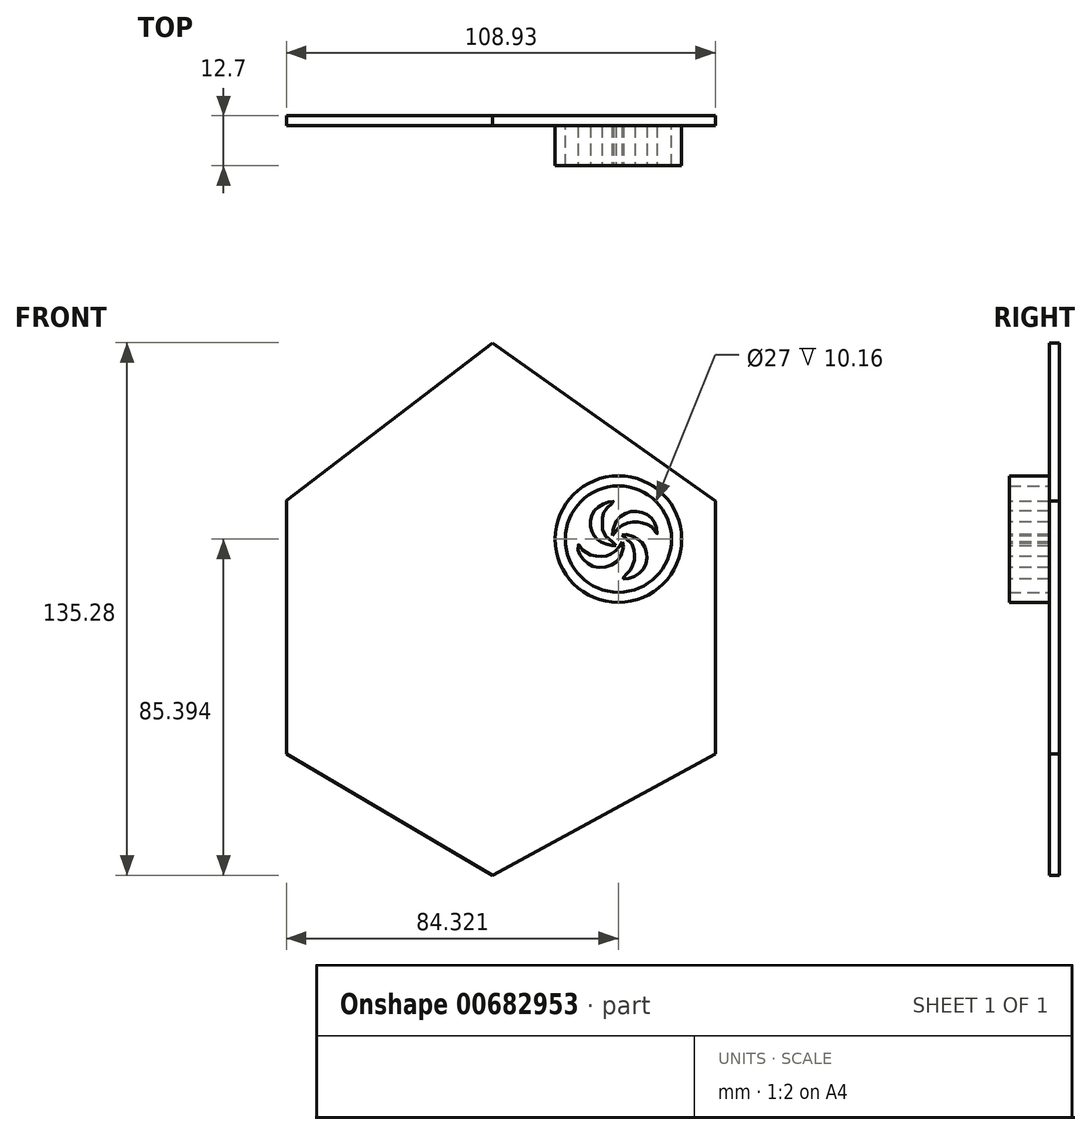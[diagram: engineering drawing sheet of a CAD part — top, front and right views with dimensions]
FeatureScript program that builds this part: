
annotation { "Feature Type Name" : "Feature", "Feature Type Description" : "" }
export const myFeature = defineFeature(function(context is Context, id is Id, definition is map)
    precondition{}
    {
        {
            var Q0;
            Q0=qCreatedBy(makeId("Front.planeOp"),FACE);
            var sketch = newSketch(context, id + "F0", { "sketchPlane" : qUnion([Q0])});
            skLineSegment(sketch, "E0", {"start": v(0, 68.56) * mm, "end": v(59.23, 26.56) * mm});
            skLineSegment(sketch, "E1", {"start": v(59.23, 26.56) * mm, "end": v(59.23, -40.56) * mm});
            skLineSegment(sketch, "E2", {"start": v(59.23, -40.56) * mm, "end": v(0, -72.79) * mm});
            skLineSegment(sketch, "E3", {"start": v(0, -72.79) * mm, "end": v(-54.78, -40.56) * mm});
            skLineSegment(sketch, "E4", {"start": v(-54.78, -40.56) * mm, "end": v(-54.78, 26.56) * mm});
            skLineSegment(sketch, "E5", {"start": v(-54.78, 26.56) * mm, "end": v(0, 68.56) * mm});
            skSolve(sketch);
        }
        {
            var Q0;
            Q0=makeQuery(id+"F0.imprint","IMPRINT",FACE,{"disambiguationData":[TD([[makeQuery(id+"F0.imprint","IMPRINT",EDGE,{"derivedFrom":sQuery(id+"F0.wireOp",EDGE,"E0")}),-1.0]])]});
            extrude(context, id + "F1", {"entities" : qUnion([Q0]), "depth" : 12.7 * mm, "offsetDistance" : 25.4 * mm});
        }
        {
            var Q0;
            Q0=makeQuery(id+"F1.opExtrude","CAP_FACE",FACE,{"disambiguationData":[OSD([sQuery(id+"F0.wireOp",EDGE,"E0"),sQuery(id+"F0.wireOp",EDGE,"E1"),sQuery(id+"F0.wireOp",EDGE,"E2"),sQuery(id+"F0.wireOp",EDGE,"E3"),sQuery(id+"F0.wireOp",EDGE,"E4"),sQuery(id+"F0.wireOp",EDGE,"E5")])],"isStart":false});
            extrude(context, id + "F2", {"entities" : qUnion([Q0]), "operationType" : NewBodyOperationType.REMOVE, "oppositeDirection" : true, "depth" : 2.54 * mm, "offsetDistance" : 25.4 * mm});
        }
        {
            var Q0;
            Q0=makeQuery(id+"F2.boolean.opBoolean","COPY",FACE,{"derivedFrom":makeQuery(id+"F2.opExtrude","CAP_FACE",FACE,{"disambiguationData":[OSD([sQuery(id+"F0.wireOp",EDGE,"E0"),sQuery(id+"F0.wireOp",EDGE,"E1"),sQuery(id+"F0.wireOp",EDGE,"E2"),sQuery(id+"F0.wireOp",EDGE,"E3"),sQuery(id+"F0.wireOp",EDGE,"E4"),sQuery(id+"F0.wireOp",EDGE,"E5")])],"isStart":false})});
            extrude(context, id + "F3", {"entities" : qUnion([Q0]), "operationType" : NewBodyOperationType.REMOVE, "oppositeDirection" : true, "depth" : 7.62 * mm, "offsetDistance" : 25.4 * mm});
        }
        {
            var Q0;
            Q0=makeQuery(id+"F1.opExtrude","SWEPT_FACE",FACE,{"disambiguationData":[OSD([sQuery(id+"F0.wireOp",EDGE,"E0")])]});
            extrude(context, id + "F4", {"entities" : qUnion([Q0]), "operationType" : NewBodyOperationType.REMOVE, "oppositeDirection" : true, "depth" : 2.54 * mm, "offsetDistance" : 25.4 * mm});
        }
        {
            var Q0;
            Q0=makeQuery(id+"F1.opExtrude","SWEPT_FACE",FACE,{"disambiguationData":[OSD([sQuery(id+"F0.wireOp",EDGE,"E5")])]});
            extrude(context, id + "F5", {"entities" : qUnion([Q0]), "operationType" : NewBodyOperationType.REMOVE, "oppositeDirection" : true, "depth" : 2.54 * mm, "offsetDistance" : 25.4 * mm});
        }
        {
            var Q0;
            Q0=makeQuery(id+"F1.opExtrude","SWEPT_FACE",FACE,{"disambiguationData":[OSD([sQuery(id+"F0.wireOp",EDGE,"E1")])]});
            extrude(context, id + "F6", {"entities" : qUnion([Q0]), "operationType" : NewBodyOperationType.REMOVE, "oppositeDirection" : true, "depth" : 2.54 * mm, "offsetDistance" : 25.4 * mm});
        }
        {
            var Q0;
            Q0=makeQuery(id+"F1.opExtrude","SWEPT_FACE",FACE,{"disambiguationData":[OSD([sQuery(id+"F0.wireOp",EDGE,"E4")])]});
            extrude(context, id + "F7", {"entities" : qUnion([Q0]), "operationType" : NewBodyOperationType.REMOVE, "oppositeDirection" : true, "depth" : 2.54 * mm, "offsetDistance" : 25.4 * mm});
        }
        {
            var Q0;
            Q0=makeQuery(id+"F1.opExtrude","SWEPT_FACE",FACE,{"disambiguationData":[OSD([sQuery(id+"F0.wireOp",EDGE,"E3")])]});
            extrude(context, id + "F8", {"entities" : qUnion([Q0]), "operationType" : NewBodyOperationType.REMOVE, "oppositeDirection" : true, "depth" : 2.54 * mm, "offsetDistance" : 25.4 * mm});
        }
        {
            var Q0;
            Q0=makeQuery(id+"F1.opExtrude","SWEPT_FACE",FACE,{"disambiguationData":[OSD([sQuery(id+"F0.wireOp",EDGE,"E2")])]});
            extrude(context, id + "F9", {"entities" : qUnion([Q0]), "operationType" : NewBodyOperationType.REMOVE, "oppositeDirection" : true, "depth" : 2.54 * mm, "offsetDistance" : 25.4 * mm});
        }
        {
            var Q0;
            Q0=makeQuery(id+"F3.boolean.opBoolean","COPY",FACE,{"derivedFrom":makeQuery(id+"F3.opExtrude","CAP_FACE",FACE,{"disambiguationData":[OSD([sQuery(id+"F0.wireOp",EDGE,"E0"),sQuery(id+"F0.wireOp",EDGE,"E1"),sQuery(id+"F0.wireOp",EDGE,"E2"),sQuery(id+"F0.wireOp",EDGE,"E3"),sQuery(id+"F0.wireOp",EDGE,"E4"),sQuery(id+"F0.wireOp",EDGE,"E5")])],"isStart":false})});
            var sketch = newSketch(context, id + "F10", { "sketchPlane" : qUnion([Q0])});
            skCircle(sketch, "E6", {"center": v(32.08, 15.52) * mm, "radius": 16.07 * mm});
            skCircle(sketch, "E7", {"center": v(32.08, 15.52) * mm, "radius": 13.5 * mm});
            skFitSpline(sketch, "E8", {"points": [v(31.43, 13.96) * mm, v(28.75, 16.4) * mm, v(27.96, 19.23) * mm, v(28.13, 21.52) * mm, v(29.24, 23.54) * mm, v(30.84, 24.99) * mm, v(30.08, 25.06) * mm, v(28.1, 24.3) * mm, v(26.32, 23.06) * mm, v(25.25, 21.3) * mm, v(24.99, 18.94) * mm, v(25.48, 17.15) * mm, v(26.3, 15.9) * mm, v(27.8, 14.74) * mm, v(29.95, 13.98) * mm, v(31.43, 13.96) * mm]});
            skFitSpline(sketch, "E9", {"points": [v(30.55, 16.4) * mm, v(31.33, 19.9) * mm, v(33.44, 21.77) * mm, v(35.5, 22.56) * mm, v(37.63, 22.42) * mm, v(39.46, 21.7) * mm, v(40.97, 20.3) * mm, v(41.74, 18.34) * mm, v(41.85, 16.77) * mm, v(41.06, 18.12) * mm, v(39.43, 19.25) * mm, v(37.72, 19.79) * mm, v(36.1, 19.9) * mm, v(34.17, 19.53) * mm, v(32.33, 18.58) * mm, v(31.15, 17.16) * mm, v(30.55, 16.4) * mm]});
            skFitSpline(sketch, "E10", {"points": [v(33, 16.56) * mm, v(35.31, 14.55) * mm, v(36.1, 12.1) * mm, v(36.22, 10.58) * mm, v(35.5, 8.43) * mm, v(34.64, 7.13) * mm, v(33.36, 5.84) * mm, v(33.18, 5.54) * mm, v(34.25, 5.43) * mm, v(36.68, 6.3) * mm, v(38.38, 7.95) * mm, v(39.25, 10.1) * mm, v(39.23, 11.95) * mm, v(38.41, 14.19) * mm, v(36.95, 15.52) * mm, v(34.75, 16.52) * mm, v(33, 16.56) * mm]});
            skFitSpline(sketch, "E11", {"points": [v(33.16, 14.81) * mm, v(33, 11.89) * mm, v(30.9, 9.24) * mm, v(28.4, 8.42) * mm, v(25.92, 8.54) * mm, v(23.97, 9.61) * mm, v(22.46, 11.42) * mm, v(21.82, 12.96) * mm, v(22, 14.36) * mm, v(22.52, 13.25) * mm, v(23.73, 12.24) * mm, v(25.01, 11.5) * mm, v(26.95, 11.14) * mm, v(28.67, 11.19) * mm, v(30.36, 11.82) * mm, v(31.94, 13.06) * mm, v(33.16, 14.81) * mm]});
            skSolve(sketch);
        }
        {
            var Q0;
            Q0=makeQuery(id+"F10.imprint","IMPRINT",FACE,{"disambiguationData":[TD([[makeQuery(id+"F10.imprint","IMPRINT",EDGE,{"derivedFrom":sQuery(id+"F10.wireOp",EDGE,"E6")}),1.0]])]});
            var Q1;
            Q1=makeQuery(id+"F10.imprint","IMPRINT",FACE,{"disambiguationData":[TD([[makeQuery(id+"F10.imprint","IMPRINT",EDGE,{"derivedFrom":sQuery(id+"F10.wireOp",EDGE,"E9")}),-1.0]])]});
            var Q2;
            Q2=makeQuery(id+"F10.imprint","IMPRINT",FACE,{"disambiguationData":[TD([[makeQuery(id+"F10.imprint","IMPRINT",EDGE,{"derivedFrom":sQuery(id+"F10.wireOp",EDGE,"E10")}),1.0]])]});
            var Q3;
            Q3=makeQuery(id+"F10.imprint","IMPRINT",FACE,{"disambiguationData":[TD([[makeQuery(id+"F10.imprint","IMPRINT",EDGE,{"derivedFrom":sQuery(id+"F10.wireOp",EDGE,"E11")}),-1.0]])]});
            var Q4;
            Q4=makeQuery(id+"F10.imprint","IMPRINT",FACE,{"disambiguationData":[TD([[makeQuery(id+"F10.imprint","IMPRINT",EDGE,{"derivedFrom":sQuery(id+"F10.wireOp",EDGE,"E8")}),1.0]])]});
            extrude(context, id + "F11", {"entities" : qUnion([Q0, Q1, Q2, Q3, Q4]), "operationType" : NewBodyOperationType.ADD, "depth" : 6.35 * mm, "offsetDistance" : 25.4 * mm});
        }
        {
            var Q0;
            Q0=makeQuery(id+"F11.opExtrude","CAP_FACE",FACE,{"disambiguationData":[OSD([sQuery(id+"F10.wireOp",EDGE,"E6"),sQuery(id+"F10.wireOp",EDGE,"E7")])],"isStart":false});
            var Q1;
            Q1=makeQuery(id+"F11.opExtrude","CAP_FACE",FACE,{"disambiguationData":[OSD([sQuery(id+"F10.wireOp",EDGE,"E9")])],"isStart":false});
            var Q2;
            Q2=makeQuery(id+"F11.opExtrude","CAP_FACE",FACE,{"disambiguationData":[OSD([sQuery(id+"F10.wireOp",EDGE,"E10")])],"isStart":false});
            var Q3;
            Q3=makeQuery(id+"F11.opExtrude","CAP_FACE",FACE,{"disambiguationData":[OSD([sQuery(id+"F10.wireOp",EDGE,"E11")])],"isStart":false});
            var Q4;
            Q4=makeQuery(id+"F11.opExtrude","CAP_FACE",FACE,{"disambiguationData":[OSD([sQuery(id+"F10.wireOp",EDGE,"E8")])],"isStart":false});
            extrude(context, id + "F12", {"entities" : qUnion([Q0, Q1, Q2, Q3, Q4]), "operationType" : NewBodyOperationType.ADD, "depth" : 2.54 * mm, "offsetDistance" : 25.4 * mm});
        }
        {
            var Q0;
            Q0=makeQuery(id+"F12.opExtrude","CAP_FACE",FACE,{"disambiguationData":[OSD([sQuery(id+"F10.wireOp",EDGE,"E6"),sQuery(id+"F10.wireOp",EDGE,"E7")])],"isStart":false});
            var Q1;
            Q1=makeQuery(id+"F12.opExtrude","CAP_FACE",FACE,{"disambiguationData":[OSD([sQuery(id+"F10.wireOp",EDGE,"E11")])],"isStart":false});
            var Q2;
            Q2=makeQuery(id+"F12.opExtrude","CAP_FACE",FACE,{"disambiguationData":[OSD([sQuery(id+"F10.wireOp",EDGE,"E8")])],"isStart":false});
            var Q3;
            Q3=makeQuery(id+"F12.opExtrude","CAP_FACE",FACE,{"disambiguationData":[OSD([sQuery(id+"F10.wireOp",EDGE,"E9")])],"isStart":false});
            var Q4;
            Q4=makeQuery(id+"F12.opExtrude","CAP_FACE",FACE,{"disambiguationData":[OSD([sQuery(id+"F10.wireOp",EDGE,"E10")])],"isStart":false});
            extrude(context, id + "F13", {"entities" : qUnion([Q0, Q1, Q2, Q3, Q4]), "operationType" : NewBodyOperationType.ADD, "depth" : 12.7 * mm, "offsetDistance" : 25.4 * mm});
        }
        {
            var Q0;
            Q0=makeQuery(id+"F13.opExtrude","CAP_FACE",FACE,{"disambiguationData":[OSD([sQuery(id+"F10.wireOp",EDGE,"E6"),sQuery(id+"F10.wireOp",EDGE,"E7")])],"isStart":false});
            var Q1;
            Q1=makeQuery(id+"F13.opExtrude","CAP_FACE",FACE,{"disambiguationData":[OSD([sQuery(id+"F10.wireOp",EDGE,"E8")])],"isStart":false});
            var Q2;
            Q2=makeQuery(id+"F13.opExtrude","CAP_FACE",FACE,{"disambiguationData":[OSD([sQuery(id+"F10.wireOp",EDGE,"E11")])],"isStart":false});
            var Q3;
            Q3=makeQuery(id+"F13.opExtrude","CAP_FACE",FACE,{"disambiguationData":[OSD([sQuery(id+"F10.wireOp",EDGE,"E9")])],"isStart":false});
            var Q4;
            Q4=makeQuery(id+"F13.opExtrude","CAP_FACE",FACE,{"disambiguationData":[OSD([sQuery(id+"F10.wireOp",EDGE,"E10")])],"isStart":false});
            extrude(context, id + "F14", {"entities" : qUnion([Q0, Q1, Q2, Q3, Q4]), "operationType" : NewBodyOperationType.REMOVE, "oppositeDirection" : true, "depth" : 15.24 * mm, "offsetDistance" : 25.4 * mm});
        }
        {
            var Q0;
            Q0=makeQuery(id+"F14.boolean.opBoolean","COPY",FACE,{"derivedFrom":makeQuery(id+"F14.opExtrude","CAP_FACE",FACE,{"disambiguationData":[OSD([sQuery(id+"F10.wireOp",EDGE,"E6"),sQuery(id+"F10.wireOp",EDGE,"E7")])],"isStart":false})});
            var Q1;
            Q1=makeQuery(id+"F14.boolean.opBoolean","COPY",FACE,{"derivedFrom":makeQuery(id+"F14.opExtrude","CAP_FACE",FACE,{"disambiguationData":[OSD([sQuery(id+"F10.wireOp",EDGE,"E9")])],"isStart":false})});
            var Q2;
            Q2=makeQuery(id+"F14.boolean.opBoolean","COPY",FACE,{"derivedFrom":makeQuery(id+"F14.opExtrude","CAP_FACE",FACE,{"disambiguationData":[OSD([sQuery(id+"F10.wireOp",EDGE,"E10")])],"isStart":false})});
            var Q3;
            Q3=makeQuery(id+"F14.boolean.opBoolean","COPY",FACE,{"derivedFrom":makeQuery(id+"F14.opExtrude","CAP_FACE",FACE,{"disambiguationData":[OSD([sQuery(id+"F10.wireOp",EDGE,"E11")])],"isStart":false})});
            var Q4;
            Q4=makeQuery(id+"F14.boolean.opBoolean","COPY",FACE,{"derivedFrom":makeQuery(id+"F14.opExtrude","CAP_FACE",FACE,{"disambiguationData":[OSD([sQuery(id+"F10.wireOp",EDGE,"E8")])],"isStart":false})});
            extrude(context, id + "F15", {"entities" : qUnion([Q0, Q1, Q2, Q3, Q4]), "operationType" : NewBodyOperationType.ADD, "depth" : 12.7 * mm, "offsetDistance" : 25.4 * mm});
        }
        {
            var Q0;
            Q0=makeQuery(id+"F15.opExtrude","CAP_FACE",FACE,{"disambiguationData":[OSD([sQuery(id+"F10.wireOp",EDGE,"E6"),sQuery(id+"F10.wireOp",EDGE,"E7")])],"isStart":false});
            var Q1;
            Q1=makeQuery(id+"F15.opExtrude","CAP_FACE",FACE,{"disambiguationData":[OSD([sQuery(id+"F10.wireOp",EDGE,"E9")])],"isStart":false});
            var Q2;
            Q2=makeQuery(id+"F15.opExtrude","CAP_FACE",FACE,{"disambiguationData":[OSD([sQuery(id+"F10.wireOp",EDGE,"E10")])],"isStart":false});
            var Q3;
            Q3=makeQuery(id+"F15.opExtrude","CAP_FACE",FACE,{"disambiguationData":[OSD([sQuery(id+"F10.wireOp",EDGE,"E11")])],"isStart":false});
            var Q4;
            Q4=makeQuery(id+"F15.opExtrude","CAP_FACE",FACE,{"disambiguationData":[OSD([sQuery(id+"F10.wireOp",EDGE,"E8")])],"isStart":false});
            extrude(context, id + "F16", {"entities" : qUnion([Q0, Q1, Q2, Q3, Q4]), "operationType" : NewBodyOperationType.REMOVE, "oppositeDirection" : true, "depth" : 7.62 * mm, "offsetDistance" : 25.4 * mm});
        }
        {
            var Q0;
            Q0=makeQuery(id+"F16.boolean.opBoolean","COPY",FACE,{"derivedFrom":makeQuery(id+"F16.opExtrude","CAP_FACE",FACE,{"disambiguationData":[OSD([sQuery(id+"F10.wireOp",EDGE,"E6"),sQuery(id+"F10.wireOp",EDGE,"E7")])],"isStart":false})});
            var Q1;
            Q1=makeQuery(id+"F16.boolean.opBoolean","COPY",FACE,{"derivedFrom":makeQuery(id+"F16.opExtrude","CAP_FACE",FACE,{"disambiguationData":[OSD([sQuery(id+"F10.wireOp",EDGE,"E8")])],"isStart":false})});
            var Q2;
            Q2=makeQuery(id+"F16.boolean.opBoolean","COPY",FACE,{"derivedFrom":makeQuery(id+"F16.opExtrude","CAP_FACE",FACE,{"disambiguationData":[OSD([sQuery(id+"F10.wireOp",EDGE,"E9")])],"isStart":false})});
            var Q3;
            Q3=makeQuery(id+"F16.boolean.opBoolean","COPY",FACE,{"derivedFrom":makeQuery(id+"F16.opExtrude","CAP_FACE",FACE,{"disambiguationData":[OSD([sQuery(id+"F10.wireOp",EDGE,"E10")])],"isStart":false})});
            var Q4;
            Q4=makeQuery(id+"F16.boolean.opBoolean","COPY",FACE,{"derivedFrom":makeQuery(id+"F16.opExtrude","CAP_FACE",FACE,{"disambiguationData":[OSD([sQuery(id+"F10.wireOp",EDGE,"E11")])],"isStart":false})});
            extrude(context, id + "F17", {"entities" : qUnion([Q0, Q1, Q2, Q3, Q4]), "operationType" : NewBodyOperationType.REMOVE, "oppositeDirection" : true, "depth" : 2.54 * mm, "offsetDistance" : 25.4 * mm});
        }
        {
            var Q0;
            Q0=makeQuery(id+"F17.boolean.opBoolean","COPY",FACE,{"derivedFrom":makeQuery(id+"F17.opExtrude","CAP_FACE",FACE,{"disambiguationData":[OSD([sQuery(id+"F10.wireOp",EDGE,"E6"),sQuery(id+"F10.wireOp",EDGE,"E7")])],"isStart":false})});
            var Q1;
            Q1=makeQuery(id+"F17.boolean.opBoolean","COPY",FACE,{"derivedFrom":makeQuery(id+"F17.opExtrude","CAP_FACE",FACE,{"disambiguationData":[OSD([sQuery(id+"F10.wireOp",EDGE,"E9")])],"isStart":false})});
            var Q2;
            Q2=makeQuery(id+"F17.boolean.opBoolean","COPY",FACE,{"derivedFrom":makeQuery(id+"F17.opExtrude","CAP_FACE",FACE,{"disambiguationData":[OSD([sQuery(id+"F10.wireOp",EDGE,"E10")])],"isStart":false})});
            var Q3;
            Q3=makeQuery(id+"F17.boolean.opBoolean","COPY",FACE,{"derivedFrom":makeQuery(id+"F17.opExtrude","CAP_FACE",FACE,{"disambiguationData":[OSD([sQuery(id+"F10.wireOp",EDGE,"E8")])],"isStart":false})});
            var Q4;
            Q4=makeQuery(id+"F17.boolean.opBoolean","COPY",FACE,{"derivedFrom":makeQuery(id+"F17.opExtrude","CAP_FACE",FACE,{"disambiguationData":[OSD([sQuery(id+"F10.wireOp",EDGE,"E11")])],"isStart":false})});
            extrude(context, id + "F18", {"entities" : qUnion([Q0, Q1, Q2, Q3, Q4]), "operationType" : NewBodyOperationType.ADD, "depth" : 1.27 * mm, "offsetDistance" : 25.4 * mm});
        }
    });
